# Revit family: ROTHOB_Rothoblaas_Plate_X-One
name_source: partatom
category: Structural Connections
units: mm (PartAtom-declared; Revit-internal decimal feet)

## family parameters
Cut with Voids When Loaded = No
Enable cutting in views = Yes
Host = Face
Material for Model Behavior = Steel
OmniClass Number = 23.13.23.11.19.13
OmniClass Title = Wood Connectors
Shared = No

## types (1)
- XONE_273x90x113mm
    BIMObjectName = ROTHOB_Rothoblaas_Plate_X-One
    CECode = ETA-15/0632
    Category = Pr_20_85_09_11: Carbon steel brackets
    CodePerformance = CE - Construction products
    Color = Silver
    Default Elevation = 1219.2 mm  [stored 4 ft]
    Description = X-RAD system connection element
    DurationUnit = Years
    Esporta tipo in formato IFC con nome = IfcDiscreteAccessoryType
    ExpectedLife = 50
    Features = Load bearing connection between CLT elements
    Finish = Zinc plated
    Height_H = 113 mm  [stored 0.370735 ft]
    IfcExportAs = IfcDiscreteAccessoryType
    IfcExportType = USERDEFINED
    Length_L = 273 mm  [stored 0.895669 ft]
    ManufacturerName = ROTHO BLAAS SRL
    ManufacturerURL = www.rothoblaas.com
    Material = Carbon steel
    MinWeight = 2.801 kg
    ModelDisclaimer = The latest version of the data sheets can be found on our website
    ModelNumber = XONE
    Name = Plate
    NominalHeight = 113 mm  [stored 0.370735 ft]
    NominalLength = 273 mm  [stored 0.895669 ft]
    NominalWidth = 90 mm  [stored 0.295276 ft]
    ObjectMaterial_Metal = ROTHOB_Rothoblaas_CarbonSteel_ZincPlated
    ObjectMaterial_Wood = ROTHOB_Rothoblaas_Wood
    OmniClassCode = 23-13 23 11 19 13
    OmniClassTitle = Wood Connectors
    OmniClassVersion = 2012-05-16
    ProductInformation = https://www.rothoblaas.com
    Revision = 1
    Shape = Three-dimensional
    Size = 273x90x113 mm
    Size_Imperial = 10 3/4x3 1/2x4 1/2 in
    Tipo IFC predefinito = USERDEFINED
    UniClass2015Code = Pr_20_85_09_11
    UniClass2015Title = Carbon steel brackets
    UniClass2015Version = Products v1.33
    Version = 2
    Width_B = 90 mm  [stored 0.295276 ft]

note: [stored X ft] marks values corroborated as IEEE doubles in the binary element streams (Revit-internal decimal feet)
